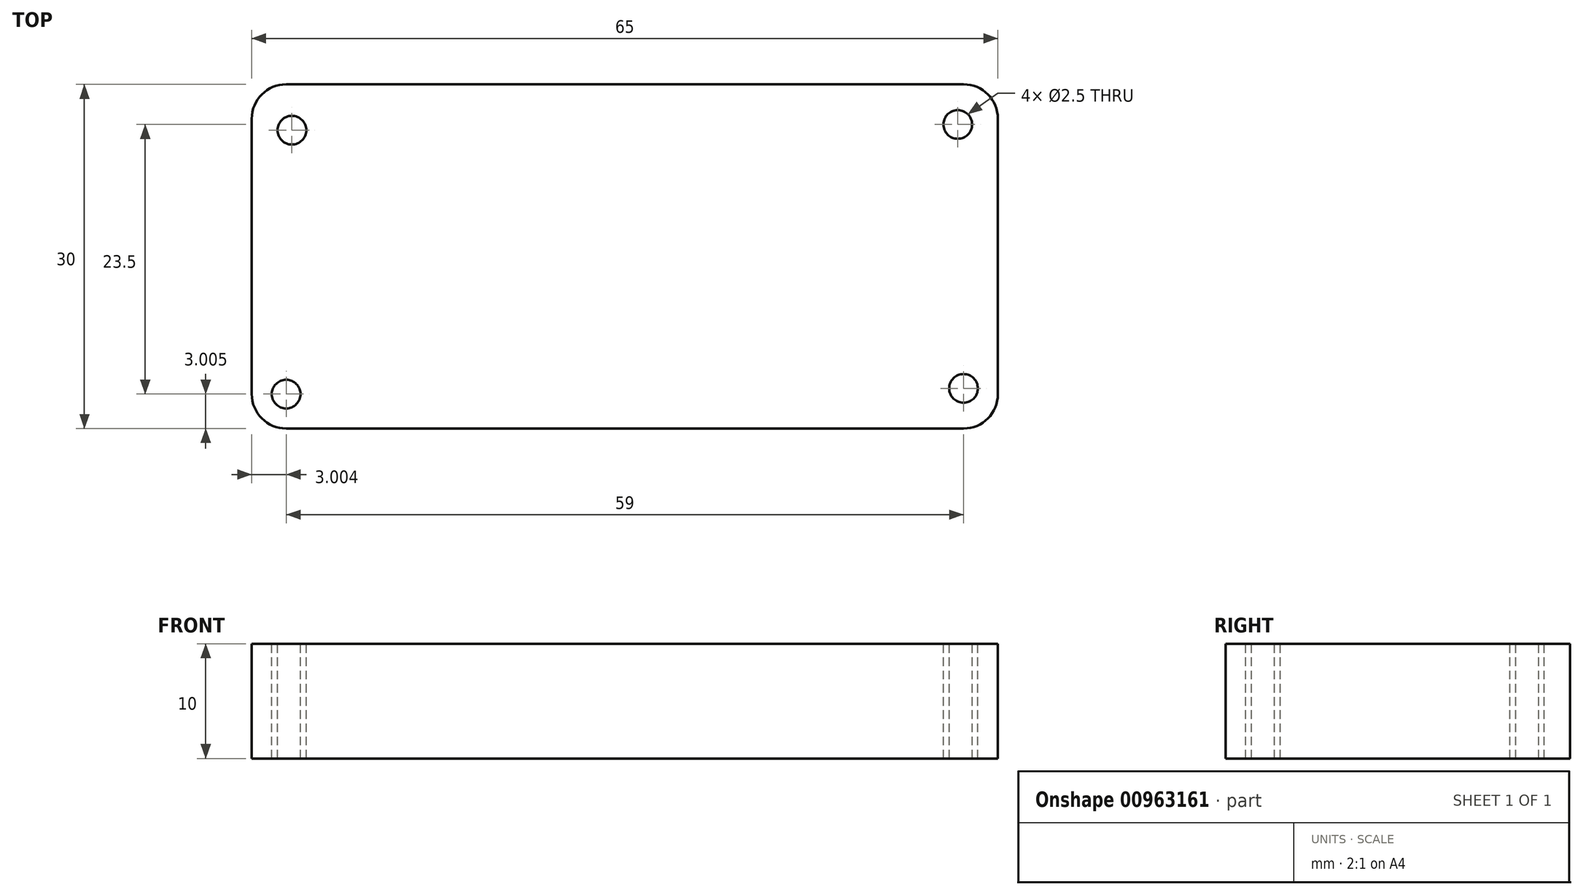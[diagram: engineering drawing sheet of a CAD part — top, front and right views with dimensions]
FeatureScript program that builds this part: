
annotation { "Feature Type Name" : "Feature", "Feature Type Description" : "" }
export const myFeature = defineFeature(function(context is Context, id is Id, definition is map)
    precondition{}
    {
        {
            var Q0;
            Q0=qCreatedBy(makeId("Top.planeOp"),FACE);
            var sketch = newSketch(context, id + "F0", { "sketchPlane" : qUnion([Q0])});
            skLineSegment(sketch, "E0.bottom", {"start": v(-35.3, 18.06) * mm, "end": v(23.7, 18.06) * mm});
            skLineSegment(sketch, "E0.top", {"start": v(-35.3, -11.94) * mm, "end": v(23.7, -11.94) * mm});
            skLineSegment(sketch, "E0.left", {"start": v(-38.3, 15.06) * mm, "end": v(-38.3, -8.94) * mm});
            skLineSegment(sketch, "E0.right", {"start": v(26.7, 15.06) * mm, "end": v(26.7, -8.94) * mm});
            skPoint(sketch, "E1.visualSharp", {"position": v(26.7, 18.06) * mm});
            skArc(sketch, "E1.filletArc", {"start": v(26.7, 15.06) * mm, "mid": v(25.82, 17.19) * mm, "end": v(23.7, 18.06) * mm});
            skPoint(sketch, "E2.visualSharp", {"position": v(26.7, -11.94) * mm});
            skArc(sketch, "E2.filletArc", {"start": v(23.7, -11.94) * mm, "mid": v(25.82, -11.06) * mm, "end": v(26.7, -8.94) * mm});
            skPoint(sketch, "E3.visualSharp", {"position": v(-38.3, -11.94) * mm});
            skArc(sketch, "E3.filletArc", {"start": v(-38.3, -8.94) * mm, "mid": v(-37.43, -11.06) * mm, "end": v(-35.3, -11.94) * mm});
            skPoint(sketch, "E4.visualSharp", {"position": v(-38.3, 18.06) * mm});
            skArc(sketch, "E4.filletArc", {"start": v(-35.3, 18.06) * mm, "mid": v(-37.43, 17.19) * mm, "end": v(-38.3, 15.06) * mm});
            skSolve(sketch);
        }
        {
            var Q0;
            Q0=makeQuery(id+"F0.imprint","IMPRINT",FACE,{"disambiguationData":[TD([[makeQuery(id+"F0.imprint","IMPRINT",EDGE,{"derivedFrom":sQuery(id+"F0.wireOp",EDGE,"E0.bottom")}),-1.0]])]});
            extrude(context, id + "F1", {"entities" : qUnion([Q0]), "depth" : 10 * mm, "offsetDistance" : 25 * mm});
        }
        {
            var Q0;
            Q0=makeQuery(id+"F1.opExtrude","CAP_FACE",FACE,{"disambiguationData":[OSD([sQuery(id+"F0.wireOp",EDGE,"E0.bottom"),sQuery(id+"F0.wireOp",EDGE,"E0.top"),sQuery(id+"F0.wireOp",EDGE,"E0.left"),sQuery(id+"F0.wireOp",EDGE,"E0.right"),sQuery(id+"F0.wireOp",EDGE,"E1.filletArc"),sQuery(id+"F0.wireOp",EDGE,"E2.filletArc"),sQuery(id+"F0.wireOp",EDGE,"E3.filletArc"),sQuery(id+"F0.wireOp",EDGE,"E4.filletArc")])],"isStart":false});
            var sketch = newSketch(context, id + "F2", { "sketchPlane" : qUnion([Q0])});
            skPoint(sketch, "E5", {"position": v(-34.8, 14.06) * mm});
            skPoint(sketch, "E6", {"position": v(23.2, 14.56) * mm});
            skPoint(sketch, "E7", {"position": v(23.7, -8.44) * mm});
            skPoint(sketch, "E8", {"position": v(-35.3, -8.94) * mm});
            skSolve(sketch);
        }
        {
            var Q0;
            Q0=sQuery(id+"F2.wireOp",VERTEX,"E5");
            var Q1;
            Q1=sQuery(id+"F2.wireOp",VERTEX,"E8");
            var Q2;
            Q2=sQuery(id+"F2.wireOp",VERTEX,"E6");
            var Q3;
            Q3=sQuery(id+"F2.wireOp",VERTEX,"E7");
            var Q4;
            Q4=makeQuery(id+"F1.opExtrude","SWEPT_BODY",BODY,{"disambiguationData":[OSD([sQuery(id+"F0.wireOp",EDGE,"E0.bottom"),sQuery(id+"F0.wireOp",EDGE,"E0.top"),sQuery(id+"F0.wireOp",EDGE,"E0.left"),sQuery(id+"F0.wireOp",EDGE,"E0.right"),sQuery(id+"F0.wireOp",EDGE,"E1.filletArc"),sQuery(id+"F0.wireOp",EDGE,"E2.filletArc"),sQuery(id+"F0.wireOp",EDGE,"E3.filletArc"),sQuery(id+"F0.wireOp",EDGE,"E4.filletArc")])]});
            hole(context, id + "F3", {"style" : HoleStyle.SIMPLE, "endStyle" : HoleEndStyle.THROUGH, "holeDiameter" : 2.5 * mm, "majorDiameter" : 5 * mm, "isTappedThrough" : true, "tappedDepth" : 1.95 * mm, "tapClearance" : 3, "locations" : qUnion([Q0, Q1, Q2, Q3]), "scope" : qUnion([Q4])});
        }
    });
